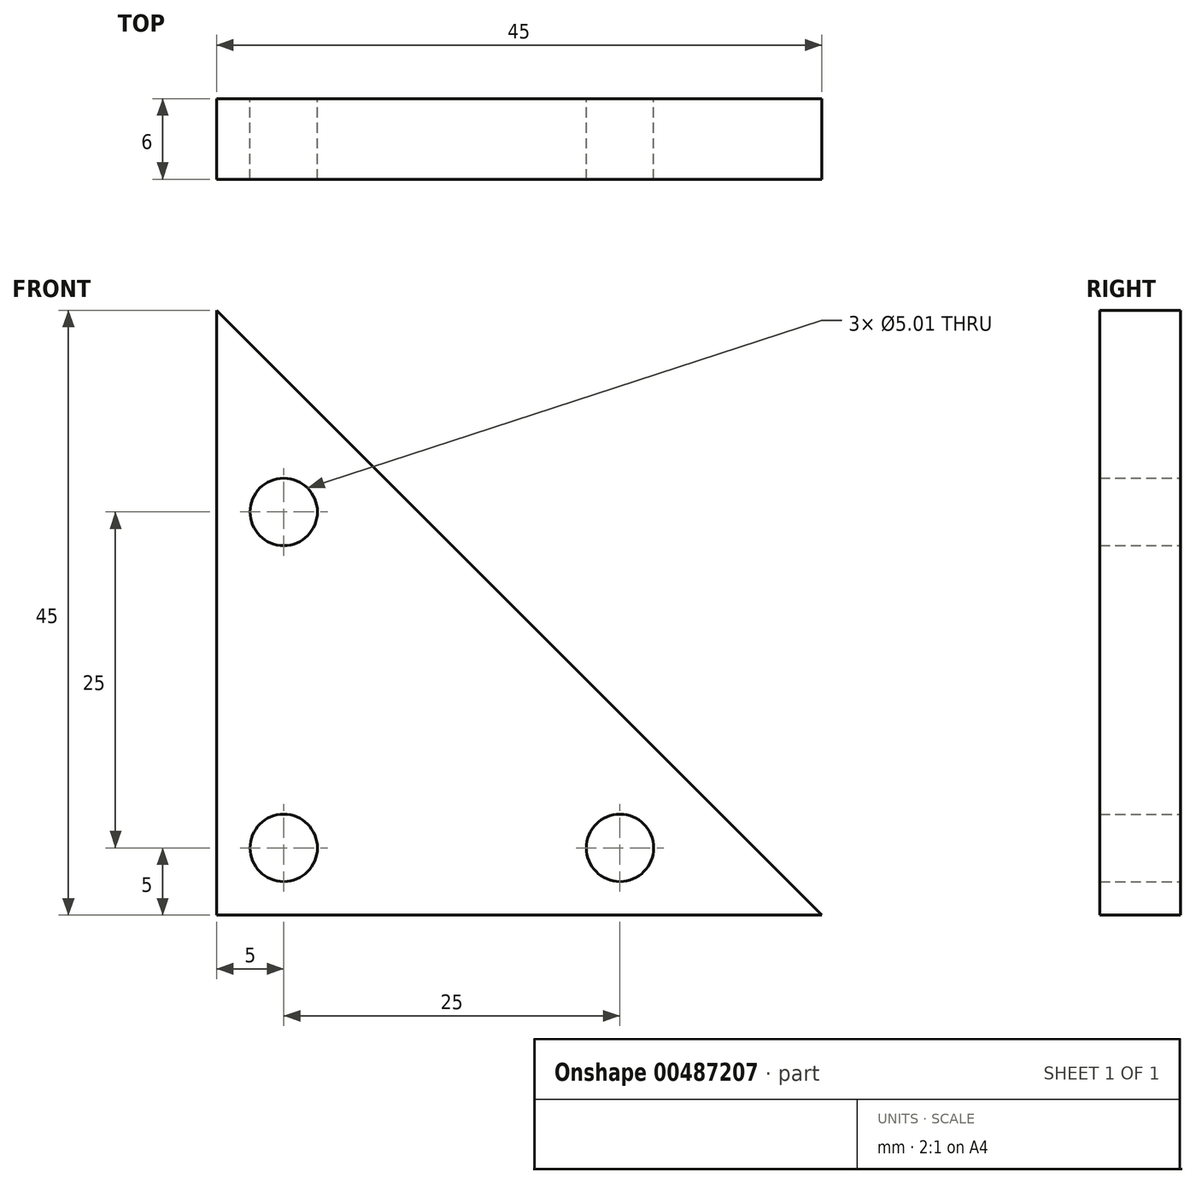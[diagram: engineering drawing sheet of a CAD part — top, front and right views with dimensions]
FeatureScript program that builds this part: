
annotation { "Feature Type Name" : "Feature", "Feature Type Description" : "" }
export const myFeature = defineFeature(function(context is Context, id is Id, definition is map)
    precondition{}
    {
        {
            var Q0;
            Q0=qCreatedBy(makeId("Front.planeOp"),FACE);
            var sketch = newSketch(context, id + "F0", { "sketchPlane" : qUnion([Q0])});
            skLineSegment(sketch, "E0", {"start": v(0, 0) * mm, "end": v(0, 45) * mm});
            skLineSegment(sketch, "E1", {"start": v(0, 45) * mm, "end": v(45, 0) * mm});
            skLineSegment(sketch, "E2", {"start": v(45, 0) * mm, "end": v(0, 0) * mm});
            skCircle(sketch, "E3", {"center": v(5, 5) * mm, "radius": 2.5 * mm});
            skCircle(sketch, "E4", {"center": v(5, 30) * mm, "radius": 2.5 * mm});
            skCircle(sketch, "E5", {"center": v(30, 5) * mm, "radius": 2.5 * mm});
            skSolve(sketch);
        }
        {
            var Q0;
            Q0=makeQuery(id+"F0.imprint","IMPRINT",FACE,{"disambiguationData":[TD([[makeQuery(id+"F0.imprint","IMPRINT",EDGE,{"derivedFrom":sQuery(id+"F0.wireOp",EDGE,"E0")}),-1.0]])]});
            extrude(context, id + "F1", {"entities" : qUnion([Q0]), "depth" : 6 * mm});
        }
    });
